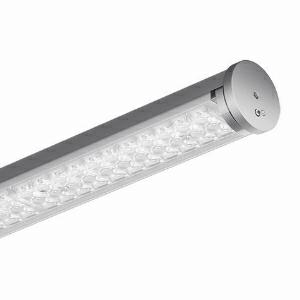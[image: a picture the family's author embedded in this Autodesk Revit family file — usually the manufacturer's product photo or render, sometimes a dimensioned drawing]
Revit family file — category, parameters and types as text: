
# Revit family: 3f_filippi_-_3f_tank_ice_extreme_medio_3f_filippi_-_52112_-_3f_tank_ice_xt_70w-840_medium_l1850
name_source: partatom
category: Lighting Fixtures
units: mm (PartAtom-declared; Revit-internal decimal feet)

## family parameters
Cut with Voids When Loaded = No
Host = Face
Light Source = No
Part Type = Normal
Room Calculation Point = No
Round Connector Dimension = Use Diameter
Shared = No

## types (1)
- 3F Filippi - 3F Tank ICE Extreme Medio (1 x LED, 10796 lm, 72 W, 4000 K)
    Apparent Load = 72 VA
    Approval mark = ENEC
    CIE Flux Codes = 69 89 97 96 100
    Color Rendering = 80
    Color Temperature = 4000 K
    Control Gear = Electronic ballast
    Default Elevation = 1800 mm
    Description = ILLUMINOTECHNICAL
Luminous efficiency 100% (DLOR 96%, ULOR 4%).
Initial luminous flux of the luminaire 10796 lm.
Direct symmetric medium distribution.
Installation Interdistance Transv.D = 1.20 x hu - Long.D = 1.19 x hu.
Tabular UGR (CIE 117 - 4H-8H; S=0.25H; 70/50/20): RUG 21 - 20.4.
Beam angle: 74° - 74°.
Luminous efficacy 150 lm/W.
Lifetime (L93/B10): 30000 h. (tq+25°C)
Lifetime (L90/B10): 50000 h. (tq+25°C)
Lifetime (L85/B10): 80000 h. (tq+25°C)
Lifetime (L80/B10): 100000 h. (tq+25°C)
Lifetime (L85/B10): 50000 h. (tq+40°C)
Sudden decreased luminous flux after 50000 hours: 0% (C0).
Photobiological safety in compliance with IEC/TR 62778: RG0 risk exempt, (IEC 62471).
In compliance with IEC/EN 62722-2-1 - IEC/EN 62717 standards.

SOURCE
Linear LED module 70W/840.
Energy efficiency class (UE 2019/2020 - UE 2019/2015): C.
CIE 13.3 Colour rendering index: CRI >80 (R9 <50%).
IES TM-30 Fidelity Index: Rf = 84 Rg = 95.
CCT nominal colour temperature 4000 K.
Colour initial tolerance (MacAdam): SDCM 3.

MECHANICAL
High thickness tubular body in high transparency polycarbonate surface treatment, which guarantees resistance to aggressive chemical agents.
Methacrylate (PMMA) lenses with external flat surface.
Die-cast aluminium end caps, painted in grey polyester.
Sealing gasket.
Gear-holder reflector in hot-dip galvanised steel, painted with white polyester base.
Fixing brackets and screws in AISI 316 stainless steel.
Dimensions: length 1852 mm, diameter 80 mm. Weight 5.17 kg.
IP69K, IP66 protection degree.
Mechanical strength to impacts IK10 (20 joule).
Glow-wire test resistance 850°C.

ELECTRICAL
Halogen Free electronic wiring 230V-50/60Hz, power factor 0.97, THD <25%, constant output current, class I, 1 driver.
Power of the luminaire 72 W.
CE - IEC 60598-1 - EN 60598-1.
Flicker: <2%.
Luminaire compliant with EN 60598-2-22 for power supply from a centralised emergency system CPSS (Central Power Supply System), not incorporated in the luminaire - high risk areas excluded. The default power and flux are 100% in AC and 100% in DC.
Ambient temperature from -30°C to +40°C.
Temperature class T6 max 85°C.
Quick connection via M20x1.5 cable gland in fibreglass reinforced polyamide with 2m H07RN-F 3G1.5mm² cable.
Relative humidity UR: <95%.

INSTALLATION
Ceiling / Suspended / Wall.
All accessories dedicated to this product are available on the Catalog and on our website www.3F-Filippi.com.

APPLICATIONS
Suitable product for food production plants (HACCP), IFS (Food Version 6), BRC (GSFS Food Version 7).
Cells with temperature from -30°C to +40°C with a humidity degree up to 95%.
Body resistant to the following substances: Ethyl alcohol (24 hours at 20°C), aqueous detergents, hydrochloric acid (produces a slight halo), DOT4 brake oil, sulfuric acid (produces a slight halo), ammonia.
Before installation, we recommend checking that there are no contraindications to the use of and polycarbonate inside the refrigerating room.
For applications in environments in which disturbances on the power network may be present and/or involve use at low temperatures, surge protection devices should be fitted on the power supply and any causes of undervoltages eliminated.
For specific applications please contact our technical offices.

WARNING
Luminaire designed for disposal/recycling at end-of-life.
Replaceable (LED only) light source by a professional. Replaceable control gear by a professional.
    Height = 80 mm  [stored 0.262467 ft]
    Lamp = 1 x LED
    Lamp Light Flux = 10796 lm
    Lamp Power = 72 W
    Lamp count = 1
    Length = 1852 mm
    Lifetime = 50000 h
    Luminous efficacy = 150 lm/W
    Manufacturer = 3F Filippi
    ModVariant = No
    Model = 3F Filippi - 52112 - 3F Tank ICE XT 70W-840 MEDIUM L1850
    Mounting Place = Ceiling
    Mounting Type = Surface mounted
    Number of Poles = 1
    OnlyDefault = Yes
    Power Factor = 1
    Product Name = 3F Filippi - 3F Tank ICE Extreme Medio
    Product group = ceiling mounted luminaire
    ProductGroupID = 3
    Protection Class = Protection class I
    Protection Degree = IP 66
    RLX_Detail_Level = 1
    RLX_Emergency_Light_Flux = 0 lm
    RLX_Emergency_Type = 0
    RLX_Emergency_Type_DB = No
    RlxData = <blob elided: 152261 chars, md5=b1f1cc03>
    Socket = socket
    Standby Power = 0 W
    System Light Flux = 10796 lm
    System Power = 72 W
    Type Comments = Product without accessories
    Type Image = 3ffilippi_3f_tank_ice_extreme_medio.jpg
    URL = http://relux.com
    VarID = ---
    Voltage = 0 V
    Weight = 0.00 kg
    Width = 80 mm  [stored 0.262467 ft]

note: [stored X ft] marks values corroborated as IEEE doubles in the binary element streams (Revit-internal decimal feet)

## geometry (parser evidence)
native form markers: Blend x4, Sweep x10
no freeform markers — native parametric forms only
